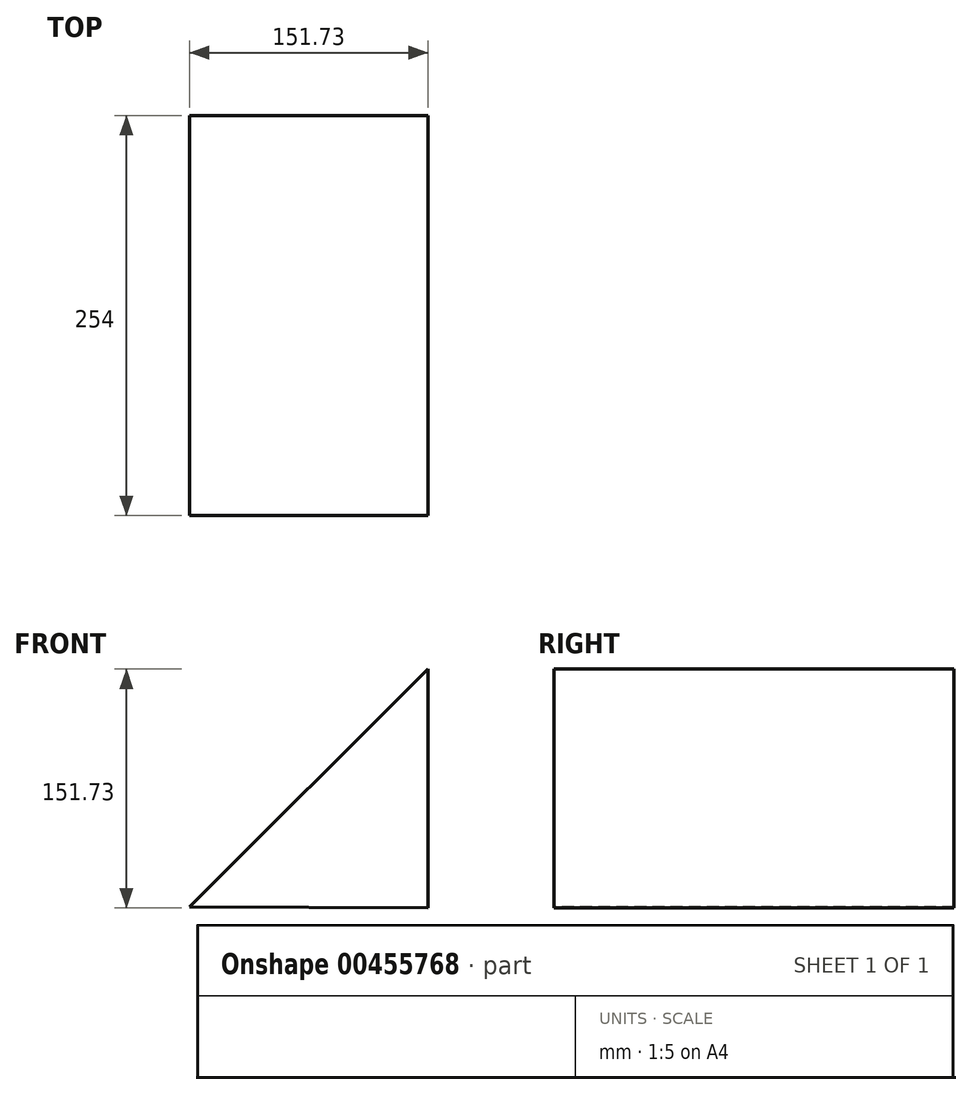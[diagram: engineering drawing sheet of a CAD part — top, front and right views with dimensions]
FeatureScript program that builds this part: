
annotation { "Feature Type Name" : "Feature", "Feature Type Description" : "" }
export const myFeature = defineFeature(function(context is Context, id is Id, definition is map)
    precondition{}
    {
        {
            var Q0;
            Q0=qCreatedBy(makeId("Front.planeOp"),FACE);
            var sketch = newSketch(context, id + "F0", { "sketchPlane" : qUnion([Q0])});
            skLineSegment(sketch, "E0", {"start": v(-75.62, -75.38) * mm, "end": v(76.1, 75.62) * mm});
            skLineSegment(sketch, "E1", {"start": v(76.1, 75.62) * mm, "end": v(76.1, -76.1) * mm});
            skLineSegment(sketch, "E2", {"start": v(76.1, -76.1) * mm, "end": v(-75.62, -75.38) * mm});
            skSolve(sketch);
        }
        {
            var Q0;
            Q0 = qSketchRegion(id + "F0", true);
            extrude(context, id + "F1", {"entities" : qUnion([Q0]), "oppositeDirection" : true, "depth" : 254 * mm});
        }
    });
